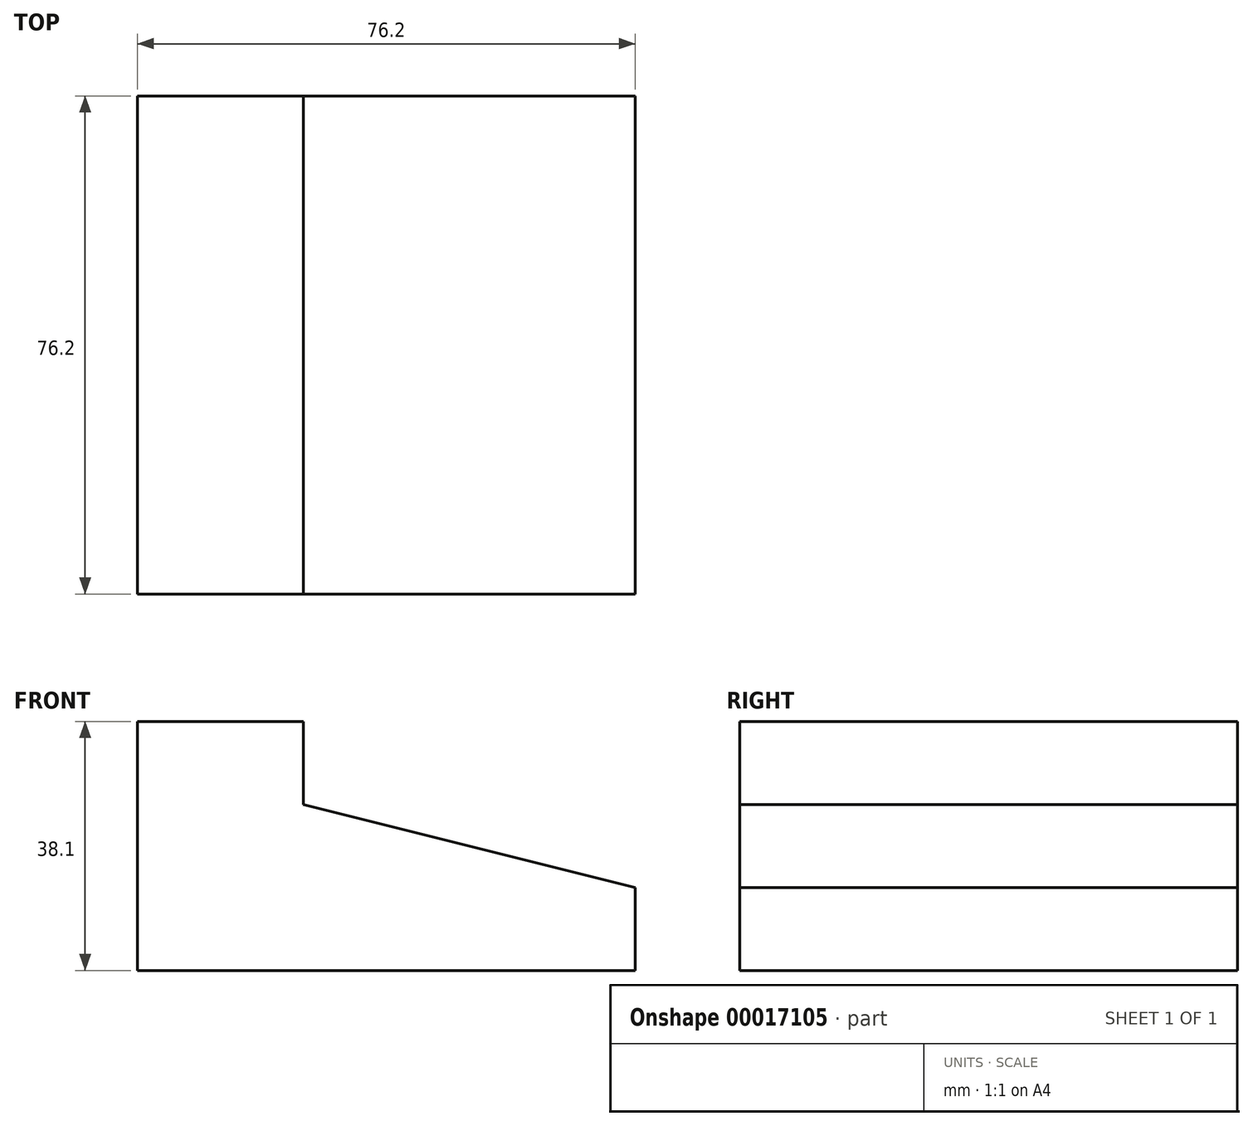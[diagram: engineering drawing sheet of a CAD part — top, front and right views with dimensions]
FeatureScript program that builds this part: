
annotation { "Feature Type Name" : "Feature", "Feature Type Description" : "" }
export const myFeature = defineFeature(function(context is Context, id is Id, definition is map)
    precondition{}
    {
        {
            var Q0;
            Q0=qCreatedBy(makeId("Front.planeOp"),FACE);
            var sketch = newSketch(context, id + "F0", { "sketchPlane" : qUnion([Q0])});
            skLineSegment(sketch, "E0", {"start": v(-32.5, 18.04) * mm, "end": v(-32.5, -20.06) * mm});
            skLineSegment(sketch, "E1", {"start": v(-32.5, -20.06) * mm, "end": v(43.7, -20.06) * mm});
            skLineSegment(sketch, "E2", {"start": v(43.7, -20.06) * mm, "end": v(43.7, -7.36) * mm});
            skLineSegment(sketch, "E3", {"start": v(43.7, -7.36) * mm, "end": v(-7.1, 5.34) * mm});
            skLineSegment(sketch, "E4", {"start": v(-32.5, 18.04) * mm, "end": v(-7.1, 18.04) * mm});
            skLineSegment(sketch, "E5", {"start": v(-7.1, 18.04) * mm, "end": v(-7.1, 5.34) * mm});
            skSolve(sketch);
        }
        {
            var Q0;
            Q0=makeQuery(id+"F0.imprint","IMPRINT",FACE,{"disambiguationData":[TD([[makeQuery(id+"F0.imprint","IMPRINT",EDGE,{"derivedFrom":sQuery(id+"F0.wireOp",EDGE,"E0")}),1.0]])]});
            extrude(context, id + "F1", {"entities" : qUnion([Q0]), "depth" : 76.2 * mm});
        }
    });
